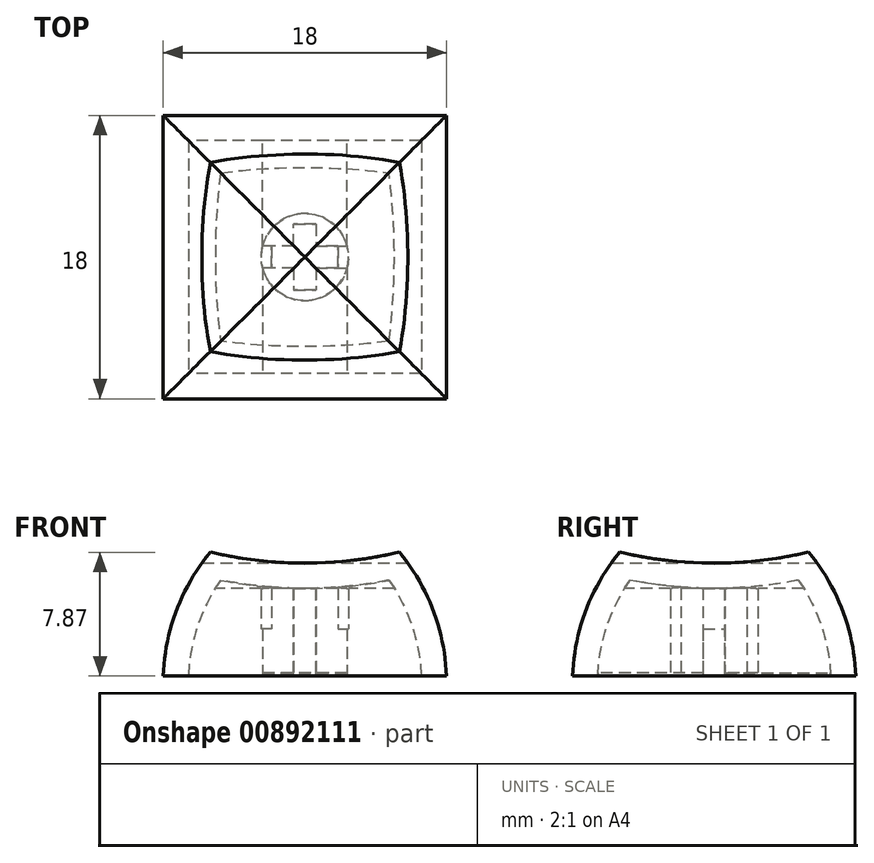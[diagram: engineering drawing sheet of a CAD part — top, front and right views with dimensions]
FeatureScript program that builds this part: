
annotation { "Feature Type Name" : "Feature", "Feature Type Description" : "" }
export const myFeature = defineFeature(function(context is Context, id is Id, definition is map)
    precondition{}
    {
        {
            var Q0;
            Q0=qCreatedBy(makeId("Top.planeOp"),FACE);
            var sketch = newSketch(context, id + "F0", { "sketchPlane" : qUnion([Q0])});
            skLineSegment(sketch, "E0.bottom", {"start": v(9, 9) * mm, "end": v(-9, 9) * mm});
            skLineSegment(sketch, "E0.top", {"start": v(9, -9) * mm, "end": v(-9, -9) * mm});
            skLineSegment(sketch, "E0.left", {"start": v(9, 9) * mm, "end": v(9, -9) * mm});
            skLineSegment(sketch, "E0.right", {"start": v(-9, 9) * mm, "end": v(-9, -9) * mm});
            skPoint(sketch, "E0.middle", {"position": v(0, 0) * mm});
            skSolve(sketch);
        }
        {
            var Q0;
            Q0=makeQuery(id+"F0.imprint","IMPRINT",FACE,{"disambiguationData":[TD([[makeQuery(id+"F0.imprint","IMPRINT",EDGE,{"derivedFrom":sQuery(id+"F0.wireOp",EDGE,"E0.bottom")}),1.0]])]});
            extrude(context, id + "F1", {"entities" : qUnion([Q0]), "depth" : 7.87 * mm, "offsetDistance" : 25 * mm});
        }
        {
            var Q0;
            Q0=makeQuery(id+"F1.opExtrude","SWEPT_FACE",FACE,{"disambiguationData":[OSD([sQuery(id+"F0.wireOp",EDGE,"E0.top")])]});
            var sketch = newSketch(context, id + "F2", { "sketchPlane" : qUnion([Q0])});
            skLineSegment(sketch, "E1", {"start": v(-9, 7.87) * mm, "end": v(-7.23, 6.1) * mm});
            skLineSegment(sketch, "E2", {"start": v(9, 7.87) * mm, "end": v(7.23, 6.1) * mm});
            skLineSegment(sketch, "E3", {"start": v(-9, 7.87) * mm, "end": v(-6, 7.87) * mm});
            skLineSegment(sketch, "E4", {"start": v(9, 7.87) * mm, "end": v(6, 7.87) * mm});
            skArc(sketch, "E5", {"start": v(-6, 7.87) * mm, "mid": v(-8.15, 4.18) * mm, "end": v(-9, 0) * mm});
            skArc(sketch, "E6", {"start": v(9, 0) * mm, "mid": v(8.15, 4.18) * mm, "end": v(6, 7.87) * mm});
            skLineSegment(sketch, "E7", {"start": v(-6, 7.87) * mm, "end": v(6, 7.87) * mm});
            skLineSegment(sketch, "E8", {"start": v(0, 7.87) * mm, "end": v(0, 7.17) * mm});
            skLineSegment(sketch, "E9", {"start": v(-6, 7.87) * mm, "end": v(-6, 7.87) * mm});
            skLineSegment(sketch, "E10", {"start": v(6, 7.87) * mm, "end": v(6, 7.87) * mm});
            skArc(sketch, "E11", {"start": v(-6, 7.87) * mm, "mid": v(0, 7.17) * mm, "end": v(6, 7.87) * mm});
            skSolve(sketch);
        }
        {
            var Q0;
            Q0=makeQuery(id+"F1.opExtrude","SWEPT_FACE",FACE,{"disambiguationData":[OSD([sQuery(id+"F0.wireOp",EDGE,"E0.right")])]});
            var sketch = newSketch(context, id + "F3", { "sketchPlane" : qUnion([Q0])});
            skLineSegment(sketch, "E12", {"start": v(-9, 7.87) * mm, "end": v(-7.23, 6.1) * mm});
            skLineSegment(sketch, "E13", {"start": v(9, 7.87) * mm, "end": v(7.23, 6.1) * mm});
            skLineSegment(sketch, "E14", {"start": v(-9, 7.87) * mm, "end": v(-6, 7.87) * mm});
            skLineSegment(sketch, "E15", {"start": v(9, 7.87) * mm, "end": v(6, 7.87) * mm});
            skArc(sketch, "E16", {"start": v(-6, 7.87) * mm, "mid": v(-8.15, 4.18) * mm, "end": v(-9, 0) * mm});
            skArc(sketch, "E17", {"start": v(9, 0) * mm, "mid": v(8.15, 4.18) * mm, "end": v(6, 7.87) * mm});
            skLineSegment(sketch, "E18", {"start": v(-6, 7.87) * mm, "end": v(-6, 7.87) * mm});
            skLineSegment(sketch, "E19", {"start": v(6, 7.87) * mm, "end": v(6, 7.87) * mm});
            skLineSegment(sketch, "E20", {"start": v(0, 7.87) * mm, "end": v(0, 7.17) * mm});
            skArc(sketch, "E21", {"start": v(-6, 7.87) * mm, "mid": v(0, 7.17) * mm, "end": v(6, 7.87) * mm});
            skSolve(sketch);
        }
        {
            var Q0;
            {var subQ0=sQuery(id+"F3.wireOp",EDGE,"E12");Q0=makeQuery(id+"F3.imprint","IMPRINT",FACE,{"disambiguationData":[TD([[makeQuery(id+"F3.imprint","IMPRINT",EDGE,{"derivedFrom":subQ0}),1.0]])]});}
            var Q1;
            {var subQ0=sQuery(id+"F3.wireOp",EDGE,"E12");Q1=makeQuery(id+"F3.imprint","IMPRINT",FACE,{"disambiguationData":[TD([[makeQuery(id+"F3.imprint","IMPRINT",EDGE,{"derivedFrom":subQ0}),-1.0]])]});}
            var Q2;
            {var subQ0=sQuery(id+"F3.wireOp",EDGE,"E20");Q2=makeQuery(id+"F3.imprint","IMPRINT",FACE,{"disambiguationData":[TD([[makeQuery(id+"F3.imprint","IMPRINT",EDGE,{"derivedFrom":subQ0}),-1.0]])]});}
            var Q3;
            {var subQ0=sQuery(id+"F3.wireOp",EDGE,"E20");Q3=makeQuery(id+"F3.imprint","IMPRINT",FACE,{"disambiguationData":[TD([[makeQuery(id+"F3.imprint","IMPRINT",EDGE,{"derivedFrom":subQ0}),1.0]])]});}
            var Q4;
            {var subQ0=sQuery(id+"F3.wireOp",EDGE,"E13");Q4=makeQuery(id+"F3.imprint","IMPRINT",FACE,{"disambiguationData":[TD([[makeQuery(id+"F3.imprint","IMPRINT",EDGE,{"derivedFrom":subQ0}),-1.0]])]});}
            var Q5;
            {var subQ0=sQuery(id+"F3.wireOp",EDGE,"E13");Q5=makeQuery(id+"F3.imprint","IMPRINT",FACE,{"disambiguationData":[TD([[makeQuery(id+"F3.imprint","IMPRINT",EDGE,{"derivedFrom":subQ0}),1.0]])]});}
            extrude(context, id + "F4", {"entities" : qUnion([Q0, Q1, Q2, Q3, Q4, Q5]), "operationType" : NewBodyOperationType.REMOVE, "oppositeDirection" : true, "depth" : 25 * mm, "offsetDistance" : 25 * mm});
        }
        {
            var Q0;
            {var subQ0=sQuery(id+"F2.wireOp",EDGE,"E1");Q0=makeQuery(id+"F2.imprint","IMPRINT",FACE,{"disambiguationData":[TD([[makeQuery(id+"F2.imprint","IMPRINT",EDGE,{"derivedFrom":subQ0}),-1.0]])]});}
            var Q1;
            {var subQ0=sQuery(id+"F2.wireOp",EDGE,"E1");Q1=makeQuery(id+"F2.imprint","IMPRINT",FACE,{"disambiguationData":[TD([[makeQuery(id+"F2.imprint","IMPRINT",EDGE,{"derivedFrom":subQ0}),1.0]])]});}
            var Q2;
            {var subQ3=sQuery(id+"F2.wireOp",EDGE,"E8");Q2=makeQuery(id+"F2.imprint","IMPRINT",FACE,{"disambiguationData":[TD([[makeQuery(id+"F2.imprint","IMPRINT",EDGE,{"derivedFrom":subQ3}),1.0]])]});}
            var Q3;
            {var subQ3=sQuery(id+"F2.wireOp",EDGE,"E8");Q3=makeQuery(id+"F2.imprint","IMPRINT",FACE,{"disambiguationData":[TD([[makeQuery(id+"F2.imprint","IMPRINT",EDGE,{"derivedFrom":subQ3}),-1.0]])]});}
            var Q4;
            {var subQ0=sQuery(id+"F2.wireOp",EDGE,"E2");Q4=makeQuery(id+"F2.imprint","IMPRINT",FACE,{"disambiguationData":[TD([[makeQuery(id+"F2.imprint","IMPRINT",EDGE,{"derivedFrom":subQ0}),-1.0]])]});}
            var Q5;
            {var subQ0=sQuery(id+"F2.wireOp",EDGE,"E2");Q5=makeQuery(id+"F2.imprint","IMPRINT",FACE,{"disambiguationData":[TD([[makeQuery(id+"F2.imprint","IMPRINT",EDGE,{"derivedFrom":subQ0}),1.0]])]});}
            extrude(context, id + "F5", {"entities" : qUnion([Q0, Q1, Q2, Q3, Q4, Q5]), "operationType" : NewBodyOperationType.REMOVE, "oppositeDirection" : true, "depth" : 25 * mm, "offsetDistance" : 25 * mm});
        }
        {
            var Q0;
            Q0=makeQuery(id+"F1.opExtrude","CAP_FACE",FACE,{"disambiguationData":[OSD([sQuery(id+"F0.wireOp",EDGE,"E0.bottom"),sQuery(id+"F0.wireOp",EDGE,"E0.top"),sQuery(id+"F0.wireOp",EDGE,"E0.left"),sQuery(id+"F0.wireOp",EDGE,"E0.right")])],"isStart":true});
            shell(context, id + "F6", {"entities" : qUnion([Q0]), "thickness" : 1.6 * mm});
        }
        {
            var Q0;
            Q0=makeQuery(id+"F1.opExtrude","CAP_FACE",FACE,{"disambiguationData":[OSD([sQuery(id+"F0.wireOp",EDGE,"E0.bottom"),sQuery(id+"F0.wireOp",EDGE,"E0.top"),sQuery(id+"F0.wireOp",EDGE,"E0.left"),sQuery(id+"F0.wireOp",EDGE,"E0.right")])],"isStart":true});
            var sketch = newSketch(context, id + "F7", { "sketchPlane" : qUnion([Q0])});
            skLineSegment(sketch, "E22.bottom", {"start": v(0, 0) * mm, "end": v(0.7, 0) * mm});
            skLineSegment(sketch, "E22.top", {"start": v(0, 2.1) * mm, "end": v(0.7, 2.1) * mm});
            skLineSegment(sketch, "E22.left", {"start": v(0, 0) * mm, "end": v(0, 2.1) * mm});
            skLineSegment(sketch, "E22.right", {"start": v(0.7, 0) * mm, "end": v(0.7, 2.1) * mm});
            skLineSegment(sketch, "E23.bottom", {"start": v(0, 0) * mm, "end": v(-0.7, 0) * mm});
            skLineSegment(sketch, "E23.top", {"start": v(0, 2.1) * mm, "end": v(-0.7, 2.1) * mm});
            skLineSegment(sketch, "E23.right", {"start": v(-0.7, 0) * mm, "end": v(-0.7, 2.1) * mm});
            skLineSegment(sketch, "E24.bottom", {"start": v(0, 0) * mm, "end": v(2.1, 0) * mm});
            skLineSegment(sketch, "E24.top", {"start": v(0, 0.7) * mm, "end": v(2.1, 0.7) * mm});
            skLineSegment(sketch, "E24.left", {"start": v(0, 0) * mm, "end": v(0, 0.7) * mm});
            skLineSegment(sketch, "E24.right", {"start": v(2.1, 0) * mm, "end": v(2.1, 0.7) * mm});
            skLineSegment(sketch, "E25.top", {"start": v(0, -0.7) * mm, "end": v(2.1, -0.7) * mm});
            skLineSegment(sketch, "E25.left", {"start": v(0, 0) * mm, "end": v(0, -0.7) * mm});
            skLineSegment(sketch, "E25.right", {"start": v(2.1, 0) * mm, "end": v(2.1, -0.7) * mm});
            skLineSegment(sketch, "E26.bottom", {"start": v(0, 0) * mm, "end": v(-2.1, 0) * mm});
            skLineSegment(sketch, "E26.top", {"start": v(0, 0.7) * mm, "end": v(-2.1, 0.7) * mm});
            skLineSegment(sketch, "E26.right", {"start": v(-2.1, 0) * mm, "end": v(-2.1, 0.7) * mm});
            skLineSegment(sketch, "E27.top", {"start": v(0, -0.7) * mm, "end": v(-2.1, -0.7) * mm});
            skLineSegment(sketch, "E27.right", {"start": v(-2.1, 0) * mm, "end": v(-2.1, -0.7) * mm});
            skLineSegment(sketch, "E28.bottom", {"start": v(-0.7, 0) * mm, "end": v(0, 0) * mm});
            skLineSegment(sketch, "E28.top", {"start": v(-0.7, -2.1) * mm, "end": v(0, -2.1) * mm});
            skLineSegment(sketch, "E28.left", {"start": v(-0.7, 0) * mm, "end": v(-0.7, -2.1) * mm});
            skLineSegment(sketch, "E28.right", {"start": v(0, 0) * mm, "end": v(0, -2.1) * mm});
            skLineSegment(sketch, "E29.bottom", {"start": v(0.7, 0) * mm, "end": v(0, 0) * mm});
            skLineSegment(sketch, "E29.top", {"start": v(0.7, -2.1) * mm, "end": v(0, -2.1) * mm});
            skLineSegment(sketch, "E29.left", {"start": v(0.7, 0) * mm, "end": v(0.7, -2.1) * mm});
            skCircle(sketch, "E30", {"center": v(0, 0) * mm, "radius": 2.77 * mm});
            skSolve(sketch);
        }
        {
            var Q0;
            {var subQ12=sQuery(id+"F7.wireOp",EDGE,"E22.top");Q0=makeQuery(id+"F7.imprint","IMPRINT",FACE,{"disambiguationData":[TD([[makeQuery(id+"F7.imprint","IMPRINT",EDGE,{"derivedFrom":subQ12}),1.0]])]});}
            extrude(context, id + "F8", {"entities" : qUnion([Q0]), "operationType" : NewBodyOperationType.ADD, "oppositeDirection" : true, "depth" : 7 * mm, "offsetDistance" : 25 * mm});
        }
        {
            var Q0;
            Q0=makeQuery(id+"F8.opExtrude","CAP_FACE",FACE,{"disambiguationData":[OSD([sQuery(id+"F7.wireOp",EDGE,"E22.top"),sQuery(id+"F7.wireOp",EDGE,"E22.right"),sQuery(id+"F7.wireOp",EDGE,"E23.top"),sQuery(id+"F7.wireOp",EDGE,"E23.right"),sQuery(id+"F7.wireOp",EDGE,"E24.top"),sQuery(id+"F7.wireOp",EDGE,"E24.right"),sQuery(id+"F7.wireOp",EDGE,"E25.top"),sQuery(id+"F7.wireOp",EDGE,"E25.right"),sQuery(id+"F7.wireOp",EDGE,"E26.top"),sQuery(id+"F7.wireOp",EDGE,"E26.right"),sQuery(id+"F7.wireOp",EDGE,"E27.top"),sQuery(id+"F7.wireOp",EDGE,"E27.right"),sQuery(id+"F7.wireOp",EDGE,"E28.top"),sQuery(id+"F7.wireOp",EDGE,"E28.left"),sQuery(id+"F7.wireOp",EDGE,"E29.top"),sQuery(id+"F7.wireOp",EDGE,"E29.left"),sQuery(id+"F7.wireOp",EDGE,"E30")])],"isStart":true});
            var sketch = newSketch(context, id + "F9", { "sketchPlane" : qUnion([Q0])});
            skLineSegment(sketch, "E31", {"start": v(-2.1, 0.7) * mm, "end": v(-2.68, 0.7) * mm});
            skLineSegment(sketch, "E32", {"start": v(-2.1, -0.7) * mm, "end": v(-2.68, -0.7) * mm});
            skLineSegment(sketch, "E33", {"start": v(2.1, -0.7) * mm, "end": v(2.68, -0.7) * mm});
            skLineSegment(sketch, "E34", {"start": v(2.1, 0.7) * mm, "end": v(2.68, 0.7) * mm});
            skCircle(sketch, "E35", {"center": v(0, 0) * mm, "radius": 2.77 * mm});
            skSolve(sketch);
        }
        {
            var Q0;
            {var subQ0=sQuery(id+"F9.wireOp",EDGE,"E31");Q0=makeQuery(id+"F9.imprint","IMPRINT",FACE,{"disambiguationData":[TD([[makeQuery(id+"F9.imprint","IMPRINT",EDGE,{"derivedFrom":subQ0}),1.0]])]});}
            var Q1;
            {var subQ0=sQuery(id+"F9.wireOp",EDGE,"E33");Q1=makeQuery(id+"F9.imprint","IMPRINT",FACE,{"disambiguationData":[TD([[makeQuery(id+"F9.imprint","IMPRINT",EDGE,{"derivedFrom":subQ0}),1.0]])]});}
            extrude(context, id + "F10", {"entities" : qUnion([Q0, Q1]), "operationType" : NewBodyOperationType.REMOVE, "oppositeDirection" : true, "depth" : 3 * mm, "offsetDistance" : 25 * mm});
        }
        {
            var Q0;
            {var subQ0=sQuery(id+"F7.wireOp",EDGE,"E24.top");var subQ1=sQuery(id+"F7.wireOp",EDGE,"E23.right");var subQ2=sQuery(id+"F7.wireOp",EDGE,"E22.right");var subQ3=sQuery(id+"F7.wireOp",EDGE,"E30");var subQ4=sQuery(id+"F7.wireOp",EDGE,"E23.top");var subQ5=sQuery(id+"F7.wireOp",EDGE,"E22.top");var subQ6=sQuery(id+"F7.wireOp",EDGE,"E26.top");Q0=makeQuery(id+"F10.boolean.opBoolean","SPLIT",FACE,{"disambiguationData":[TD([makeQuery(id+"F8.opExtrude","SWEPT_FACE",FACE,{"disambiguationData":[OSD([subQ2])]})])],"derivedFrom":makeQuery(id+"F8.opExtrude","CAP_FACE",FACE,{"disambiguationData":[OSD([subQ5,subQ2,subQ4,subQ1,subQ0,sQuery(id+"F7.wireOp",EDGE,"E24.right"),sQuery(id+"F7.wireOp",EDGE,"E25.top"),sQuery(id+"F7.wireOp",EDGE,"E25.right"),subQ6,sQuery(id+"F7.wireOp",EDGE,"E26.right"),sQuery(id+"F7.wireOp",EDGE,"E27.top"),sQuery(id+"F7.wireOp",EDGE,"E27.right"),sQuery(id+"F7.wireOp",EDGE,"E28.top"),sQuery(id+"F7.wireOp",EDGE,"E28.left"),sQuery(id+"F7.wireOp",EDGE,"E29.top"),sQuery(id+"F7.wireOp",EDGE,"E29.left"),subQ3])],"isStart":true})});}
            var sketch = newSketch(context, id + "F11", { "sketchPlane" : qUnion([Q0])});
            skLineSegment(sketch, "E36", {"start": v(2.68, 0.7) * mm, "end": v(2.68, 6.7) * mm});
            skLineSegment(sketch, "E37", {"start": v(-2.68, 0.7) * mm, "end": v(-2.68, 6.7) * mm});
            skLineSegment(sketch, "E38", {"start": v(-2.68, 6.7) * mm, "end": v(2.68, 6.7) * mm});
            skLineSegment(sketch, "E39", {"start": v(-2.68, 0.7) * mm, "end": v(-2.68, -0.7) * mm});
            skLineSegment(sketch, "E40", {"start": v(-2.68, -0.7) * mm, "end": v(2.68, -0.7) * mm});
            skLineSegment(sketch, "E41", {"start": v(2.68, -0.7) * mm, "end": v(2.68, -6.7) * mm});
            skLineSegment(sketch, "E42", {"start": v(-2.68, -0.7) * mm, "end": v(-2.68, -6.7) * mm});
            skLineSegment(sketch, "E43", {"start": v(-2.68, -6.7) * mm, "end": v(2.68, -6.7) * mm});
            skLineSegment(sketch, "E44", {"start": v(-2.68, 0.7) * mm, "end": v(-0.7, 0.7) * mm});
            skLineSegment(sketch, "E45", {"start": v(-0.7, 0.7) * mm, "end": v(-0.7, 2.1) * mm});
            skLineSegment(sketch, "E46", {"start": v(-0.7, 2.1) * mm, "end": v(0.7, 2.1) * mm});
            skLineSegment(sketch, "E47", {"start": v(0.7, 2.1) * mm, "end": v(0.7, 0.7) * mm});
            skLineSegment(sketch, "E48", {"start": v(0.7, 0.7) * mm, "end": v(2.68, 0.7) * mm});
            skLineSegment(sketch, "E49", {"start": v(2.68, -0.7) * mm, "end": v(0.7, -0.7) * mm});
            skLineSegment(sketch, "E50", {"start": v(0.7, -0.7) * mm, "end": v(0.7, -2.1) * mm});
            skLineSegment(sketch, "E51", {"start": v(-2.68, -0.7) * mm, "end": v(-0.7, -0.7) * mm});
            skLineSegment(sketch, "E52", {"start": v(-0.7, -0.7) * mm, "end": v(-0.7, -2.1) * mm});
            skLineSegment(sketch, "E53", {"start": v(-0.7, -2.1) * mm, "end": v(0.7, -2.1) * mm});
            skSolve(sketch);
        }
        {
            var Q0;
            Q0=makeQuery(id+"F11.imprint","IMPRINT",FACE,{"disambiguationData":[TD([[makeQuery(id+"F11.imprint","IMPRINT",EDGE,{"derivedFrom":sQuery(id+"F11.wireOp",EDGE,"E36")}),1.0]])]});
            var Q1;
            Q1=makeQuery(id+"F11.imprint","IMPRINT",FACE,{"disambiguationData":[TD([[makeQuery(id+"F11.imprint","IMPRINT",EDGE,{"derivedFrom":sQuery(id+"F11.wireOp",EDGE,"E41")}),-1.0]])]});
            extrude(context, id + "F12", {"entities" : qUnion([Q0, Q1]), "operationType" : NewBodyOperationType.ADD, "oppositeDirection" : true, "depth" : .2 * mm, "offsetDistance" : 25 * mm});
        }
        {
            var Q0;
            Q0=makeQuery(id+"F12.opExtrude","SWEPT_FACE",FACE,{"disambiguationData":[OSD([sQuery(id+"F11.wireOp",EDGE,"E38")])]});
            extrude(context, id + "F13", {"entities" : qUnion([Q0]), "operationType" : NewBodyOperationType.ADD, "depth" : 1 * mm, "offsetDistance" : 25 * mm});
        }
        {
            var Q0;
            Q0=makeQuery(id+"F12.opExtrude","SWEPT_FACE",FACE,{"disambiguationData":[OSD([sQuery(id+"F11.wireOp",EDGE,"E43")])]});
            extrude(context, id + "F14", {"entities" : qUnion([Q0]), "operationType" : NewBodyOperationType.ADD, "depth" : 1 * mm, "offsetDistance" : 25 * mm});
        }
    });
